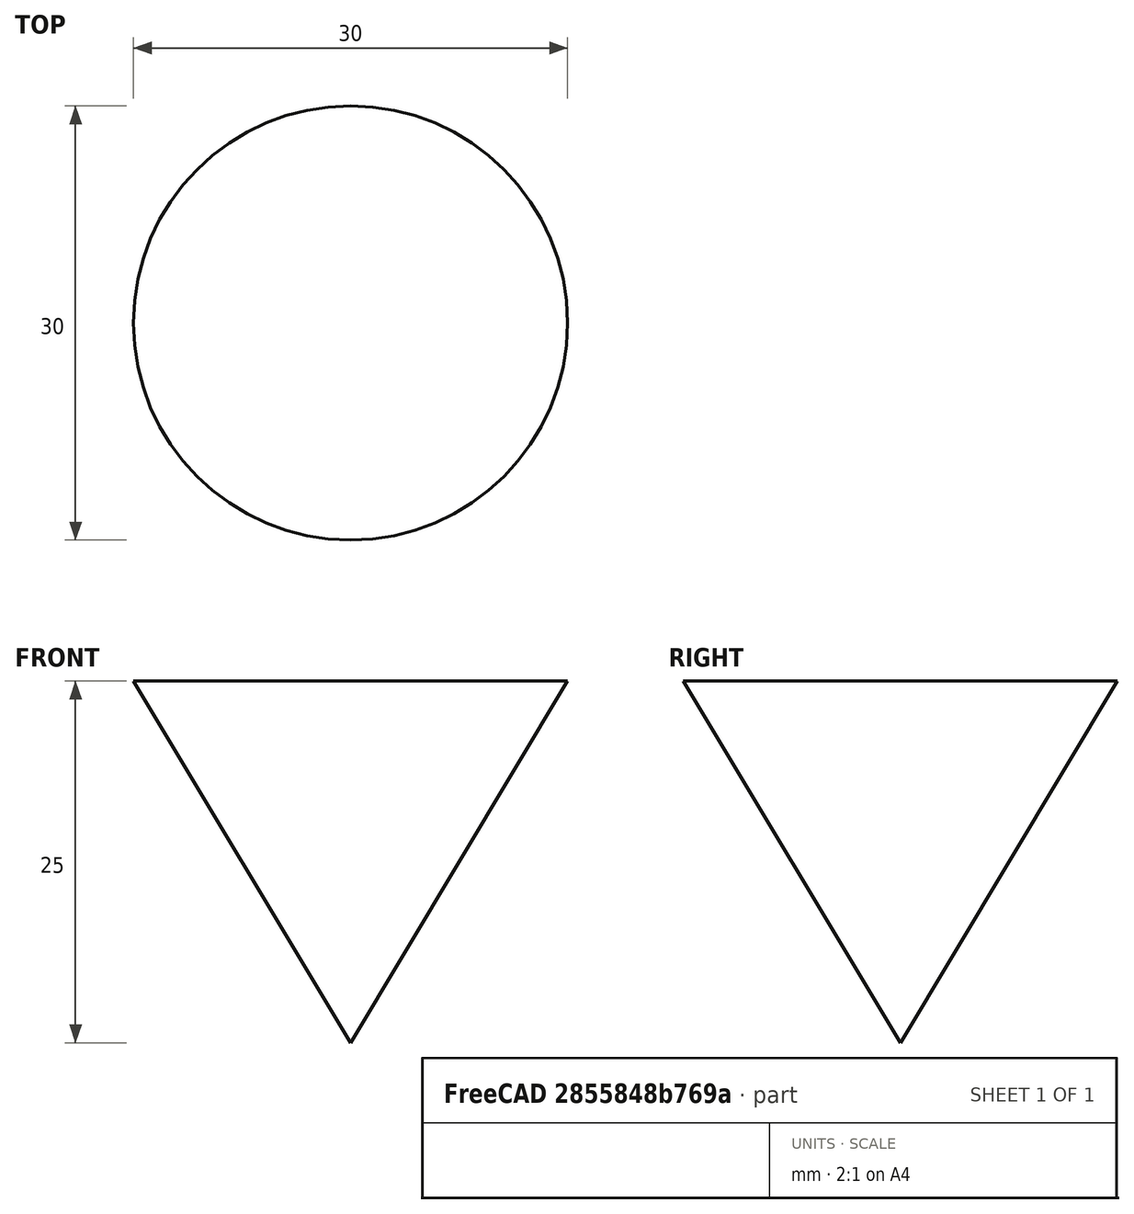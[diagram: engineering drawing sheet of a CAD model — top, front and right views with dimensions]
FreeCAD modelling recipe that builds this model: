
FCSTD DOCUMENT  (FreeCAD 0.18.4R)
Label: tool
License: All rights reserved
LicenseURL: http://en.wikipedia.org/wiki/All_rights_reserved
objects: Sketcher::SketchObject×1, PartDesign::Revolution×1, PartDesign::Body×1
note: 4 computed .brp shape members not serialized (recipe doc carries the construction recipe); baked Part::Feature solids carry a one-line shape summary decoded from their .brp

FEATURE [Sketcher::SketchObject] Sketch
  MapMode = 5
  Placement = pos=(0,0,0) rot=(1,0,0;1.5708rad)
  Support = -> [XZ_Plane]
  sketch-geometry (3):
    g0: LineSegment StartX=-15 StartY=0 StartZ=0 EndX=0 EndY=0 EndZ=0
    g1: LineSegment StartX=-15 StartY=0 StartZ=0 EndX=1.8e-15 EndY=-25 EndZ=0
    g2: LineSegment StartX=0 StartY=0 StartZ=0 EndX=1.8e-15 EndY=-25 EndZ=0
  constraints (8):
    c: Coincident(g0,g-1)
    c: DistanceY(g0,g0) = 0
    c: DistanceX(g0,g0) = 15
    c: Coincident(g1,g0)
    c: DistanceX(g1,g0) = 0
    c: DistanceY(g1,g0) = 25
    c: Coincident(g1,g2)
    c: Coincident(g2,g0)
FEATURE [PartDesign::Revolution] Revolution
  Angle = 360
  Axis = (0,2e-16,1)
  Base = (0,0,0)
  Placement = pos=(0,0,0) rot=(1,0,0;1.5708rad)
  Profile = -> Sketch
  ReferenceAxis = -> Sketch [V_Axis]
FEATURE [PartDesign::Body] Body
  Group = -> [Sketch,Revolution]
  Origin = -> Origin
  Tip = -> Revolution
